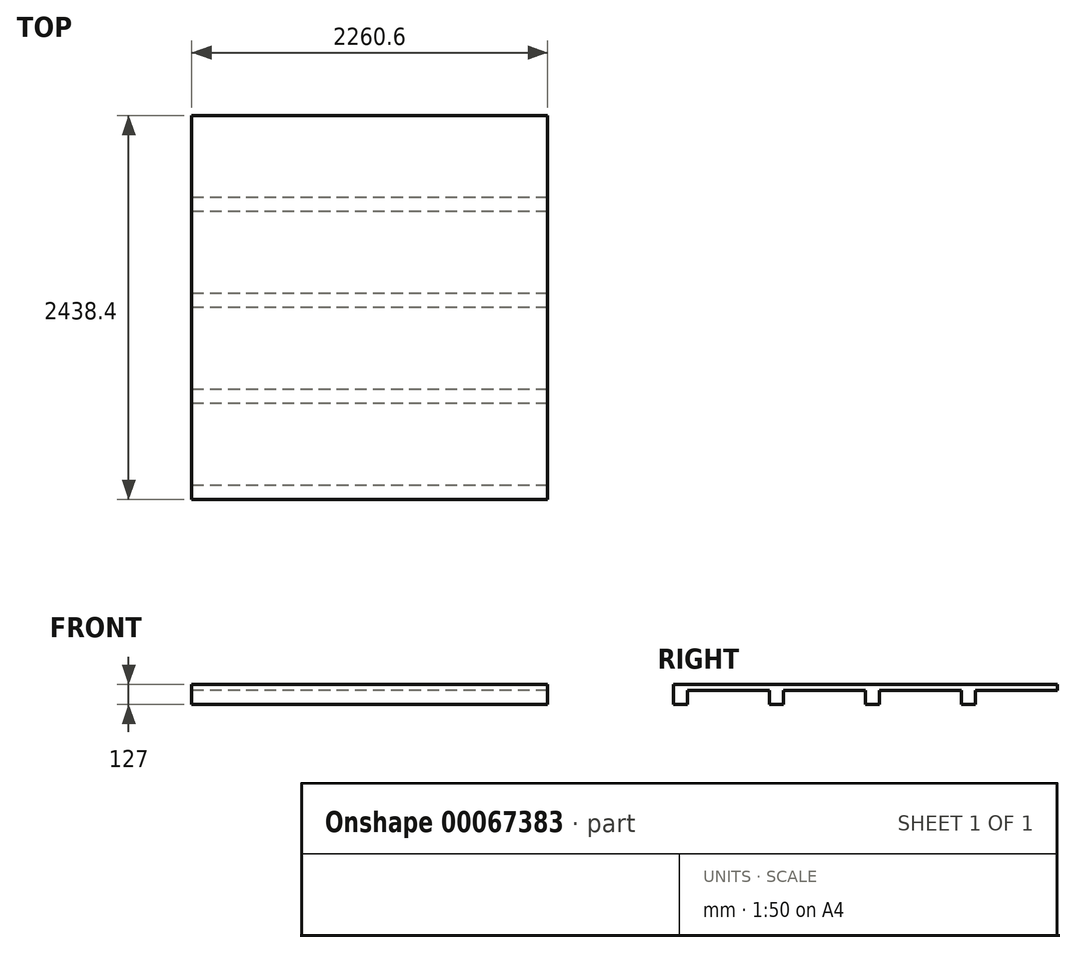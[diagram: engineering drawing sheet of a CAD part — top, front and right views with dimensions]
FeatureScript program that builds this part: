
annotation { "Feature Type Name" : "Feature", "Feature Type Description" : "" }
export const myFeature = defineFeature(function(context is Context, id is Id, definition is map)
    precondition{}
    {
        {
            var Q0;
            Q0=qCreatedBy(makeId("Top.planeOp"),FACE);
            var sketch = newSketch(context, id + "F0", { "sketchPlane" : qUnion([Q0])});
            skLineSegment(sketch, "E0.bottom", {"start": v(0, 0) * mm, "end": v(2260.6, 0) * mm});
            skLineSegment(sketch, "E0.top", {"start": v(0, -2438.4) * mm, "end": v(2260.6, -2438.4) * mm});
            skLineSegment(sketch, "E0.left", {"start": v(0, 0) * mm, "end": v(0, -2438.4) * mm});
            skLineSegment(sketch, "E0.right", {"start": v(2260.6, 0) * mm, "end": v(2260.6, -2438.4) * mm});
            skSolve(sketch);
        }
        {
            var Q0;
            Q0 = qSketchRegion(id + "F0", true);
            extrude(context, id + "F1", {"entities" : qUnion([Q0]), "depth" : 88.9 * mm + 38.1 * mm});
        }
        {
            var Q0;
            Q0=makeQuery(id+"F1.opExtrude","SWEPT_FACE",FACE,{"disambiguationData":[OSD([sQuery(id+"F0.wireOp",EDGE,"E0.left")])]});
            var sketch = newSketch(context, id + "F2", { "sketchPlane" : qUnion([Q0])});
            skLineSegment(sketch, "E1.bottom", {"start": v(0, 0) * mm, "end": v(520.7, 0) * mm});
            skLineSegment(sketch, "E1.top", {"start": v(0, 88.9) * mm, "end": v(520.7, 88.9) * mm});
            skLineSegment(sketch, "E1.left", {"start": v(0, 0) * mm, "end": v(0, 88.9) * mm});
            skLineSegment(sketch, "E1.right", {"start": v(520.7, 0) * mm, "end": v(520.7, 88.9) * mm});
            skLineSegment(sketch, "E2.bottom", {"start": v(609.6, 0) * mm, "end": v(1130.3, 0) * mm});
            skLineSegment(sketch, "E2.top", {"start": v(609.6, 88.9) * mm, "end": v(1130.3, 88.9) * mm});
            skLineSegment(sketch, "E2.left", {"start": v(609.6, 0) * mm, "end": v(609.6, 88.9) * mm});
            skLineSegment(sketch, "E2.right", {"start": v(1130.3, 0) * mm, "end": v(1130.3, 88.9) * mm});
            skLineSegment(sketch, "E3.bottom", {"start": v(1219.2, 0) * mm, "end": v(1739.9, 0) * mm});
            skLineSegment(sketch, "E3.top", {"start": v(1219.2, 88.9) * mm, "end": v(1739.9, 88.9) * mm});
            skLineSegment(sketch, "E3.left", {"start": v(1219.2, 0) * mm, "end": v(1219.2, 88.9) * mm});
            skLineSegment(sketch, "E3.right", {"start": v(1739.9, 0) * mm, "end": v(1739.9, 88.9) * mm});
            skLineSegment(sketch, "E4.bottom", {"start": v(1828.8, 0) * mm, "end": v(2349.5, 0) * mm});
            skLineSegment(sketch, "E4.top", {"start": v(1828.8, 88.9) * mm, "end": v(2349.5, 88.9) * mm});
            skLineSegment(sketch, "E4.left", {"start": v(1828.8, 0) * mm, "end": v(1828.8, 88.9) * mm});
            skLineSegment(sketch, "E4.right", {"start": v(2349.5, 0) * mm, "end": v(2349.5, 88.9) * mm});
            skLineSegment(sketch, "E5", {"start": v(520.7, 0) * mm, "end": v(609.6, 0) * mm, "construction": true});
            skLineSegment(sketch, "E6", {"start": v(1130.3, 0) * mm, "end": v(1219.2, 0) * mm, "construction": true});
            skLineSegment(sketch, "E7", {"start": v(1739.9, 0) * mm, "end": v(1828.8, 0) * mm, "construction": true});
            skLineSegment(sketch, "E8", {"start": v(2349.5, 0) * mm, "end": v(2438.4, 0) * mm, "construction": true});
            skSolve(sketch);
        }
        {
            var Q0;
            Q0 = qSketchRegion(id + "F2", true);
            extrude(context, id + "F3", {"entities" : qUnion([Q0]), "operationType" : NewBodyOperationType.REMOVE, "endBound" : BoundingType.THROUGH_ALL, "oppositeDirection" : true, "depth" : 25.4 * mm});
        }
    });
